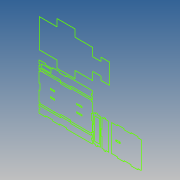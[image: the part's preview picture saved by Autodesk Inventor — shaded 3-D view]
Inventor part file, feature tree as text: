
AUTODESK INVENTOR PART (.ipt)
format: ipt  version: 2020 (Build 240168000, 168)  size: 143,872 bytes
history: native  units: mm
features: sketch x1
ambient origin geometry x8: Origin, YZ Plane, XZ Plane, XY Plane, X Axis, Y Axis, Z Axis, Center Point
feature tree (1):
  sketch  "Sketch1"
